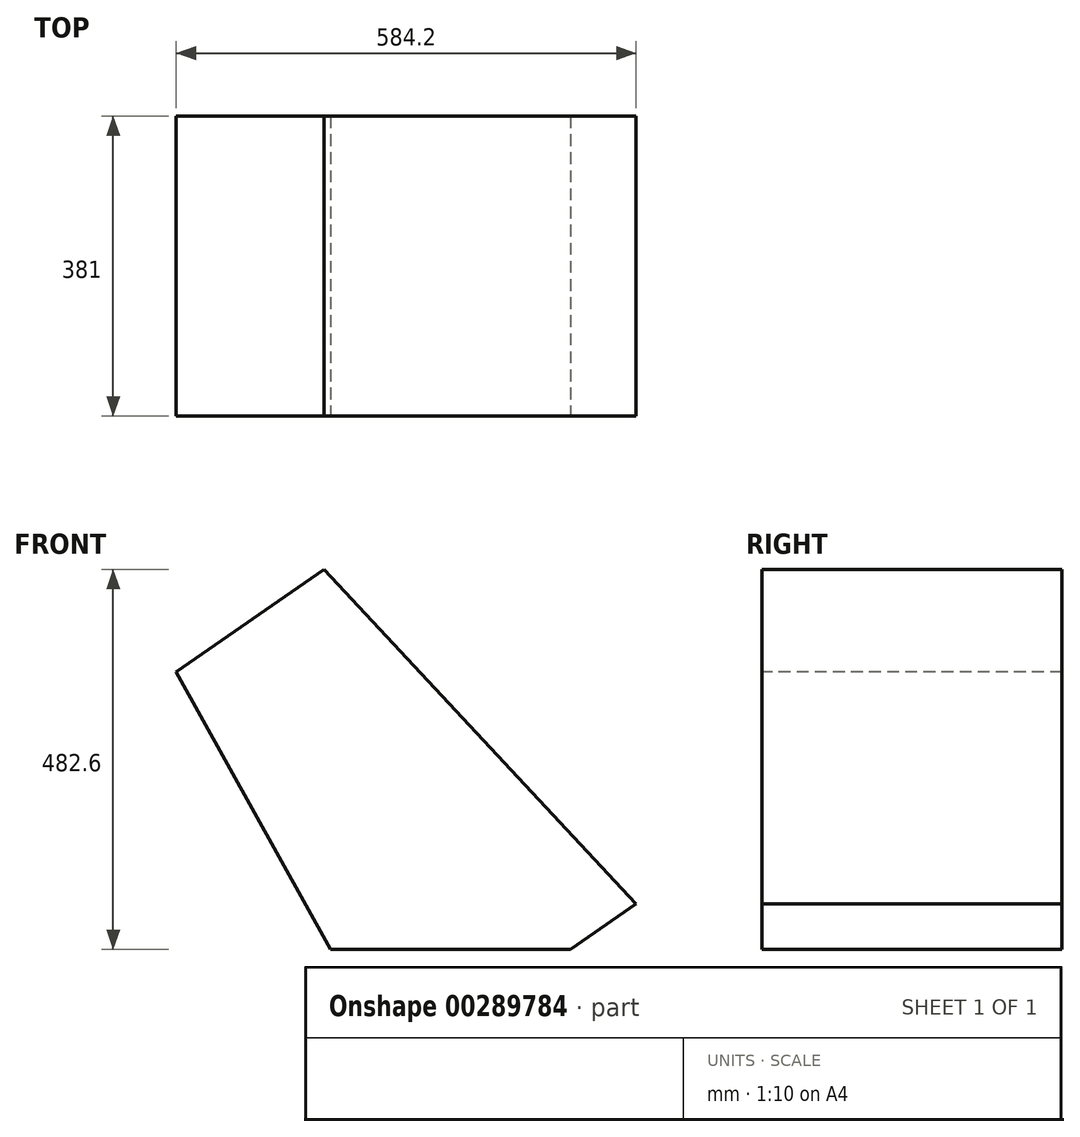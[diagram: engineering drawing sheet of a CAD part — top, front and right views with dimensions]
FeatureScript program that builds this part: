
annotation { "Feature Type Name" : "Feature", "Feature Type Description" : "" }
export const myFeature = defineFeature(function(context is Context, id is Id, definition is map)
    precondition{}
    {
        {
            var Q0;
            Q0=qCreatedBy(makeId("Front.planeOp"),FACE);
            var sketch = newSketch(context, id + "F0", { "sketchPlane" : qUnion([Q0])});
            skLineSegment(sketch, "E0", {"start": v(0, 352.38) * mm, "end": v(195.9, 0) * mm});
            skLineSegment(sketch, "E1", {"start": v(195.9, 0) * mm, "end": v(500.7, 0) * mm});
            skLineSegment(sketch, "E2", {"start": v(500.7, 0) * mm, "end": v(584.2, 57.88) * mm});
            skLineSegment(sketch, "E3", {"start": v(584.2, 57.88) * mm, "end": v(187.88, 482.6) * mm});
            skLineSegment(sketch, "E4", {"start": v(187.88, 482.6) * mm, "end": v(0, 352.38) * mm});
            skSolve(sketch);
        }
        {
            var Q0;
            Q0=makeQuery(id+"F0.imprint","IMPRINT",FACE,{"disambiguationData":[TD([[makeQuery(id+"F0.imprint","IMPRINT",EDGE,{"derivedFrom":sQuery(id+"F0.wireOp",EDGE,"E0")}),1.0]])]});
            extrude(context, id + "F1", {"entities" : qUnion([Q0]), "oppositeDirection" : true, "depth" : 381 * mm});
        }
    });
